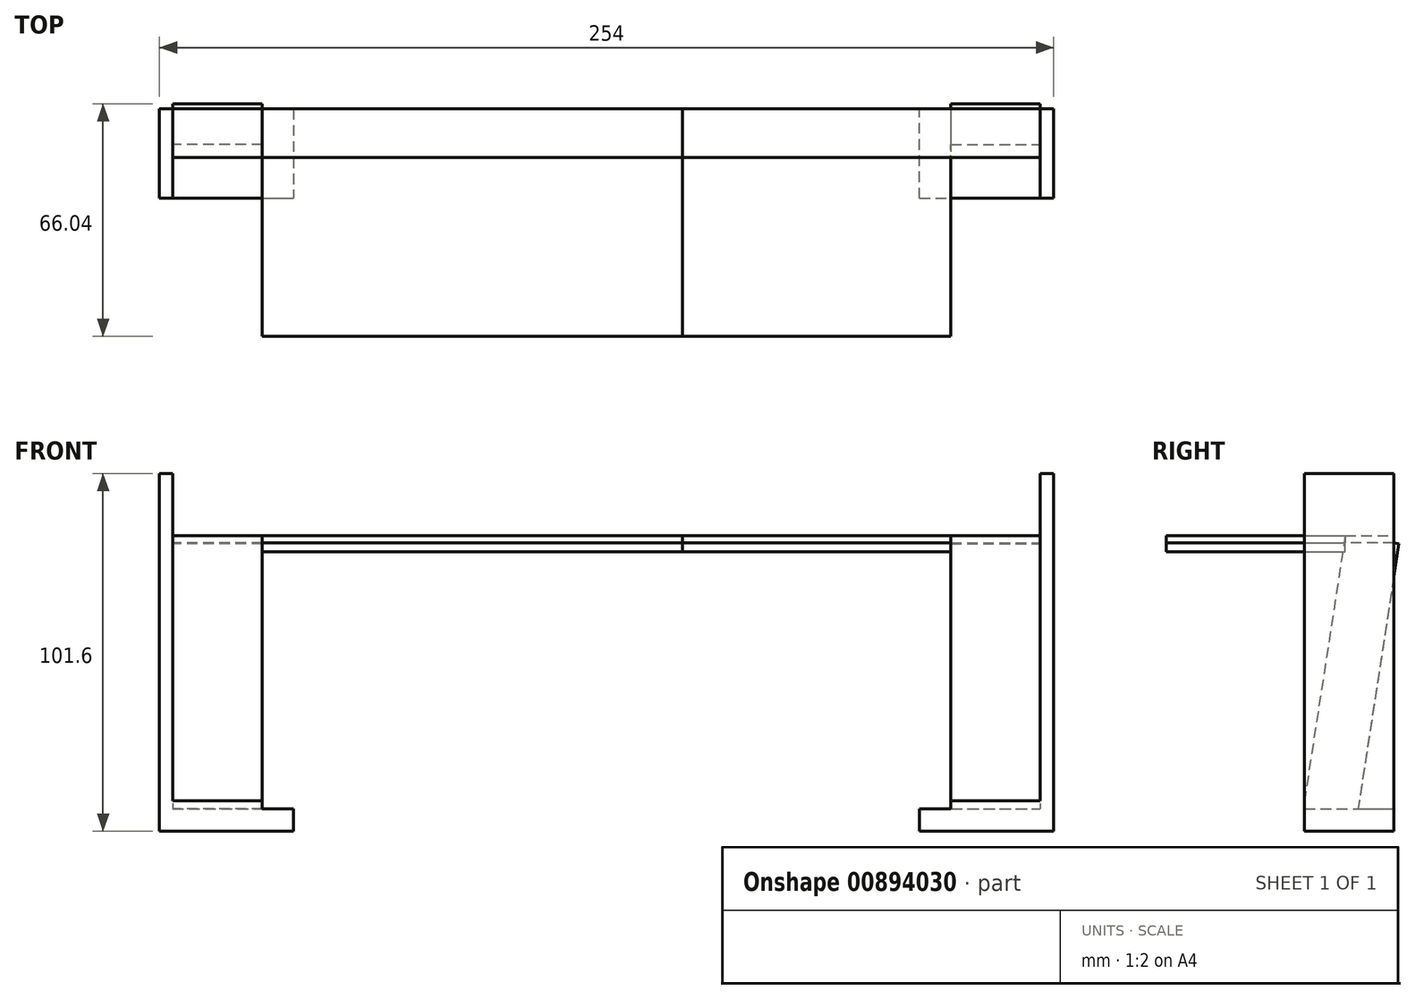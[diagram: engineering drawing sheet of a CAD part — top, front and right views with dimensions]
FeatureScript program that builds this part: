
annotation { "Feature Type Name" : "Feature", "Feature Type Description" : "" }
export const myFeature = defineFeature(function(context is Context, id is Id, definition is map)
    precondition{}
    {
        {
            var Q0;
            Q0=qCreatedBy(makeId("Top.planeOp"),FACE);
            var sketch = newSketch(context, id + "F0", { "sketchPlane" : qUnion([Q0])});
            skLineSegment(sketch, "E0.bottom", {"start": v(-148.04, 0) * mm, "end": v(-109.94, 0) * mm});
            skLineSegment(sketch, "E0.top", {"start": v(-148.04, -25.4) * mm, "end": v(-109.94, -25.4) * mm});
            skLineSegment(sketch, "E0.left", {"start": v(-148.04, 0) * mm, "end": v(-148.04, -25.4) * mm});
            skLineSegment(sketch, "E0.right", {"start": v(-109.94, 0) * mm, "end": v(-109.94, -25.4) * mm});
            skLineSegment(sketch, "E1", {"start": v(-109.94, -25.4) * mm, "end": v(67.86, -25.4) * mm});
            skLineSegment(sketch, "E2.bottom", {"start": v(67.86, -25.4) * mm, "end": v(105.96, -25.4) * mm});
            skLineSegment(sketch, "E2.top", {"start": v(67.86, 0) * mm, "end": v(105.96, 0) * mm});
            skLineSegment(sketch, "E2.left", {"start": v(67.86, -25.4) * mm, "end": v(67.86, 0) * mm});
            skLineSegment(sketch, "E2.right", {"start": v(105.96, -25.4) * mm, "end": v(105.96, 0) * mm});
            skLineSegment(sketch, "E3", {"start": v(-144.23, -12.7) * mm, "end": v(-144.23, 0) * mm});
            skLineSegment(sketch, "E4", {"start": v(-144.23, -12.7) * mm, "end": v(-144.23, -25.4) * mm});
            skLineSegment(sketch, "E5", {"start": v(102.15, -18.45) * mm, "end": v(102.15, 0) * mm});
            skLineSegment(sketch, "E6", {"start": v(102.15, -18.45) * mm, "end": v(102.15, -25.4) * mm});
            skSolve(sketch);
        }
        {
            var Q0;
            Q0=makeQuery(id+"F0.imprint","IMPRINT",FACE,{"disambiguationData":[TD([[makeQuery(id+"F0.imprint","IMPRINT",EDGE,{"derivedFrom":sQuery(id+"F0.wireOp",EDGE,"E0.bottom")}),-1.0]])]});
            extrude(context, id + "F1", {"entities" : qUnion([Q0]), "depth" : 6.35 * mm, "offsetDistance" : 25.4 * mm});
        }
        {
            var Q0;
            Q0=makeQuery(id+"F0.imprint","IMPRINT",FACE,{"disambiguationData":[TD([[makeQuery(id+"F0.imprint","IMPRINT",EDGE,{"derivedFrom":sQuery(id+"F0.wireOp",EDGE,"E2.bottom")}),1.0]])]});
            extrude(context, id + "F2", {"entities" : qUnion([Q0]), "depth" : 6.35 * mm, "offsetDistance" : 25.4 * mm});
        }
        {
            var Q0;
            {var subQ0=sQuery(id+"F0.wireOp",EDGE,"E0.left");Q0=makeQuery(id+"F0.imprint","IMPRINT",FACE,{"disambiguationData":[TD([[makeQuery(id+"F0.imprint","IMPRINT",EDGE,{"derivedFrom":subQ0}),1.0]])]});}
            extrude(context, id + "F3", {"entities" : qUnion([Q0]), "operationType" : NewBodyOperationType.ADD, "depth" : 25.4 * mm, "offsetDistance" : 25.4 * mm});
        }
        {
            var Q0;
            {var subQ0=sQuery(id+"F0.wireOp",EDGE,"E2.right");Q0=makeQuery(id+"F0.imprint","IMPRINT",FACE,{"disambiguationData":[TD([[makeQuery(id+"F0.imprint","IMPRINT",EDGE,{"derivedFrom":subQ0}),1.0]])]});}
            extrude(context, id + "F4", {"entities" : qUnion([Q0]), "operationType" : NewBodyOperationType.ADD, "depth" : 25.4 * mm, "offsetDistance" : 25.4 * mm});
        }
        {
            var Q0;
            Q0=makeQuery(id+"F3.opExtrude","SWEPT_FACE",FACE,{"disambiguationData":[OSD([sQuery(id+"F0.wireOp",EDGE,"E3"),sQuery(id+"F0.wireOp",EDGE,"E4")])]});
            var sketch = newSketch(context, id + "F5", { "sketchPlane" : qUnion([Q0])});
            skLineSegment(sketch, "E7", {"start": v(0, 6.35) * mm, "end": v(-10.16, 6.35) * mm});
            skLineSegment(sketch, "E8", {"start": v(-25.4, 6.35) * mm, "end": v(-20.32, 6.35) * mm});
            skLineSegment(sketch, "E9", {"start": v(-10.16, 6.35) * mm, "end": v(-25.4, 8.7) * mm});
            skSolve(sketch);
        }
        {
            var Q0;
            {var subQ0=sQuery(id+"F5.wireOp",EDGE,"E8");Q0=makeQuery(id+"F5.imprint","IMPRINT",FACE,{"disambiguationData":[TD([[makeQuery(id+"F5.imprint","IMPRINT",EDGE,{"derivedFrom":subQ0}),1.0]])]});}
            extrude(context, id + "F6", {"entities" : qUnion([Q0]), "operationType" : NewBodyOperationType.ADD, "depth" : 25.4 * mm, "offsetDistance" : 25.4 * mm});
        }
        {
            var Q0;
            Q0=makeQuery(id+"F4.opExtrude","SWEPT_FACE",FACE,{"disambiguationData":[OSD([sQuery(id+"F0.wireOp",EDGE,"E5"),sQuery(id+"F0.wireOp",EDGE,"E6")])]});
            var sketch = newSketch(context, id + "F7", { "sketchPlane" : qUnion([Q0])});
            skLineSegment(sketch, "E10", {"start": v(0, 6.35) * mm, "end": v(10.16, 6.35) * mm});
            skLineSegment(sketch, "E11", {"start": v(10.16, 6.35) * mm, "end": v(25.4, 8.7) * mm});
            skSolve(sketch);
        }
        {
            var Q0;
            {var subQ0=sQuery(id+"F7.wireOp",EDGE,"E11");Q0=makeQuery(id+"F7.imprint","IMPRINT",FACE,{"disambiguationData":[TD([[makeQuery(id+"F7.imprint","IMPRINT",EDGE,{"derivedFrom":subQ0}),-1.0]])]});}
            extrude(context, id + "F8", {"entities" : qUnion([Q0]), "operationType" : NewBodyOperationType.ADD, "depth" : 25.4 * mm, "offsetDistance" : 25.4 * mm});
        }
        {
            var Q0;
            Q0=makeQuery(id+"F6.opExtrude","SWEPT_FACE",FACE,{"disambiguationData":[OSD([sQuery(id+"F5.wireOp",EDGE,"E9")])]});
            var sketch = newSketch(context, id + "F9", { "sketchPlane" : qUnion([Q0])});
            skSolve(sketch);
        }
        {
            var Q0;
            Q0=makeQuery(id+"F8.opExtrude","SWEPT_FACE",FACE,{"disambiguationData":[OSD([sQuery(id+"F7.wireOp",EDGE,"E11")])]});
            var sketch = newSketch(context, id + "F10", { "sketchPlane" : qUnion([Q0])});
            skSolve(sketch);
        }
        {
            var Q0;
            {var subQ0=sQuery(id+"F7.wireOp",EDGE,"E11");Q0=makeQuery(id+"F10.imprint","IMPRINT",FACE,{"disambiguationData":[TD([[makeQuery(id+"F10.imprint","IMPRINT",EDGE,{"derivedFrom":makeQuery(id+"F8.opExtrude","CAP_EDGE",EDGE,{"disambiguationData":[OSD([subQ0])],"isStart":false})}),1.0]])]});}
            extrude(context, id + "F11", {"entities" : qUnion([Q0]), "operationType" : NewBodyOperationType.ADD, "depth" : 76.2 * mm, "offsetDistance" : 25.4 * mm});
        }
        {
            var Q0;
            {var subQ0=sQuery(id+"F5.wireOp",EDGE,"E9");Q0=makeQuery(id+"F9.imprint","IMPRINT",FACE,{"disambiguationData":[TD([[makeQuery(id+"F9.imprint","IMPRINT",EDGE,{"derivedFrom":makeQuery(id+"F6.opExtrude","CAP_EDGE",EDGE,{"disambiguationData":[OSD([subQ0])],"isStart":false})}),-1.0]])]});}
            extrude(context, id + "F12", {"entities" : qUnion([Q0]), "operationType" : NewBodyOperationType.ADD, "depth" : 76.2 * mm, "offsetDistance" : 25.4 * mm});
        }
        {
            var Q0;
            Q0=makeQuery(id+"F4.opExtrude","CAP_FACE",FACE,{"disambiguationData":[OSD([sQuery(id+"F0.wireOp",EDGE,"E2.bottom"),sQuery(id+"F0.wireOp",EDGE,"E2.top"),sQuery(id+"F0.wireOp",EDGE,"E2.right"),sQuery(id+"F0.wireOp",EDGE,"E5"),sQuery(id+"F0.wireOp",EDGE,"E6")])],"isStart":false});
            var sketch = newSketch(context, id + "F13", { "sketchPlane" : qUnion([Q0])});
            skSolve(sketch);
        }
        {
            var Q0;
            {var subQ4=sQuery(id+"F0.wireOp",EDGE,"E2.bottom");Q0=makeQuery(id+"F13.imprint","IMPRINT",FACE,{"disambiguationData":[TD([[makeQuery(id+"F13.imprint","IMPRINT",EDGE,{"derivedFrom":makeQuery(id+"F4.opExtrude","CAP_EDGE",EDGE,{"disambiguationData":[OSD([subQ4])],"isStart":false})}),1.0]])]});}
            extrude(context, id + "F14", {"entities" : qUnion([Q0]), "operationType" : NewBodyOperationType.ADD, "depth" : 76.2 * mm, "offsetDistance" : 25.4 * mm});
        }
        {
            var Q0;
            Q0=makeQuery(id+"F3.opExtrude","CAP_FACE",FACE,{"disambiguationData":[OSD([sQuery(id+"F0.wireOp",EDGE,"E0.bottom"),sQuery(id+"F0.wireOp",EDGE,"E0.top"),sQuery(id+"F0.wireOp",EDGE,"E0.left"),sQuery(id+"F0.wireOp",EDGE,"E3"),sQuery(id+"F0.wireOp",EDGE,"E4")])],"isStart":false});
            var sketch = newSketch(context, id + "F15", { "sketchPlane" : qUnion([Q0])});
            skSolve(sketch);
        }
        {
            var Q0;
            {var subQ4=sQuery(id+"F0.wireOp",EDGE,"E0.bottom");Q0=makeQuery(id+"F15.imprint","IMPRINT",FACE,{"disambiguationData":[TD([[makeQuery(id+"F15.imprint","IMPRINT",EDGE,{"derivedFrom":makeQuery(id+"F3.opExtrude","CAP_EDGE",EDGE,{"disambiguationData":[OSD([subQ4])],"isStart":false})}),-1.0]])]});}
            extrude(context, id + "F16", {"entities" : qUnion([Q0]), "operationType" : NewBodyOperationType.ADD, "depth" : 76.2 * mm, "offsetDistance" : 25.4 * mm});
        }
        {
            var Q0;
            {var subQ0=sQuery(id+"F0.wireOp",EDGE,"E6");var subQ1=sQuery(id+"F0.wireOp",EDGE,"E5");var subQ2=sQuery(id+"F0.wireOp",EDGE,"E2.bottom");Q0=makeQuery(id+"F14.boolean.opBoolean","MERGE",FACE,{"derivedFrom":[makeQuery(id+"F11.boolean.opBoolean","SPLIT",FACE,{"disambiguationData":[TD([makeQuery(id+"F2.opExtrude","SWEPT_FACE",FACE,{"disambiguationData":[OSD([subQ2])]})])],"derivedFrom":makeQuery(id+"F4.opExtrude","SWEPT_FACE",FACE,{"disambiguationData":[OSD([subQ1,subQ0])]})}),makeQuery(id+"F14.opExtrude","SWEPT_FACE",FACE,{"disambiguationData":[OSD([subQ1,subQ0])]})]});}
            var sketch = newSketch(context, id + "F17", { "sketchPlane" : qUnion([Q0])});
            skLineSegment(sketch, "E12", {"start": v(13.8, 84) * mm, "end": v(0, 84) * mm});
            skLineSegment(sketch, "E13", {"start": v(0, 84) * mm, "end": v(0, 81.88) * mm});
            skSolve(sketch);
        }
        {
            var Q0;
            Q0=makeQuery(id+"F17.imprint","IMPRINT",FACE,{"disambiguationData":[TD([[makeQuery(id+"F17.imprint","IMPRINT",EDGE,{"derivedFrom":sQuery(id+"F17.wireOp",EDGE,"E12")}),1.0]])]});
            extrude(context, id + "F18", {"entities" : qUnion([Q0]), "operationType" : NewBodyOperationType.ADD, "depth" : 25.4 * mm, "offsetDistance" : 25.4 * mm});
        }
        {
            var Q0;
            {var subQ0=sQuery(id+"F0.wireOp",EDGE,"E4");var subQ1=sQuery(id+"F0.wireOp",EDGE,"E3");var subQ2=sQuery(id+"F0.wireOp",EDGE,"E0.top");Q0=makeQuery(id+"F16.boolean.opBoolean","MERGE",FACE,{"derivedFrom":[makeQuery(id+"F12.boolean.opBoolean","SPLIT",FACE,{"disambiguationData":[TD([makeQuery(id+"F1.opExtrude","SWEPT_FACE",FACE,{"disambiguationData":[OSD([subQ2])]})])],"derivedFrom":makeQuery(id+"F3.opExtrude","SWEPT_FACE",FACE,{"disambiguationData":[OSD([subQ1,subQ0])]})}),makeQuery(id+"F16.opExtrude","SWEPT_FACE",FACE,{"disambiguationData":[OSD([subQ1,subQ0])]})]});}
            var sketch = newSketch(context, id + "F19", { "sketchPlane" : qUnion([Q0])});
            skLineSegment(sketch, "E14", {"start": v(0, 84) * mm, "end": v(0, 81.88) * mm});
            skLineSegment(sketch, "E15", {"start": v(0, 84) * mm, "end": v(-13.8, 84) * mm});
            skSolve(sketch);
        }
        {
            var Q0;
            {var subQ0=sQuery(id+"F7.wireOp",EDGE,"E11");Q0=makeQuery(id+"F18.boolean.opBoolean","MERGE",FACE,{"derivedFrom":[makeQuery(id+"F11.boolean.opBoolean","MERGE",FACE,{"derivedFrom":[makeQuery(id+"F8.opExtrude","CAP_FACE",FACE,{"disambiguationData":[OSD([sQuery(id+"F0.wireOp",EDGE,"E2.bottom"),sQuery(id+"F0.wireOp",EDGE,"E2.top"),sQuery(id+"F0.wireOp",EDGE,"E2.left"),sQuery(id+"F0.wireOp",EDGE,"E2.right"),sQuery(id+"F0.wireOp",EDGE,"E5"),sQuery(id+"F0.wireOp",EDGE,"E6"),subQ0])],"isStart":false}),makeQuery(id+"F11.opExtrude","SWEPT_FACE",FACE,{"disambiguationData":[OSD([subQ0]),TDD([makeQuery(id+"F10.imprint","IMPRINT",EDGE,{"derivedFrom":makeQuery(id+"F8.opExtrude","CAP_EDGE",EDGE,{"disambiguationData":[OSD([subQ0])],"isStart":false})})])]})]}),makeQuery(id+"F18.opExtrude","CAP_FACE",FACE,{"disambiguationData":[OSD([subQ0,sQuery(id+"F17.wireOp",EDGE,"E12"),sQuery(id+"F17.wireOp",EDGE,"E13")])],"isStart":false})]});}
            var sketch = newSketch(context, id + "F20", { "sketchPlane" : qUnion([Q0])});
            skLineSegment(sketch, "E16", {"start": v(0, 81.88) * mm, "end": v(13.8, 81.88) * mm});
            skLineSegment(sketch, "E17", {"start": v(0, 81.88) * mm, "end": v(0, 84) * mm});
            skLineSegment(sketch, "E18", {"start": v(0, 84) * mm, "end": v(13.8, 84) * mm});
            skLineSegment(sketch, "E19", {"start": v(13.8, 84) * mm, "end": v(13.8, 81.88) * mm});
            skSolve(sketch);
        }
        {
            var Q0;
            Q0 = qSketchRegion(id + "F20", true);
            extrude(context, id + "F21", {"entities" : qUnion([Q0]), "operationType" : NewBodyOperationType.ADD, "depth" : 76.2 * mm, "offsetDistance" : 25.4 * mm});
        }
        {
            var Q0;
            Q0=makeQuery(id+"F19.imprint","IMPRINT",FACE,{"disambiguationData":[TD([[makeQuery(id+"F19.imprint","IMPRINT",EDGE,{"derivedFrom":sQuery(id+"F19.wireOp",EDGE,"E14")}),-1.0]])]});
            extrude(context, id + "F22", {"entities" : qUnion([Q0]), "operationType" : NewBodyOperationType.ADD, "depth" : 25.4 * mm, "offsetDistance" : 25.4 * mm});
        }
        {
            var Q0;
            {var subQ0=sQuery(id+"F5.wireOp",EDGE,"E9");Q0=makeQuery(id+"F22.boolean.opBoolean","MERGE",FACE,{"derivedFrom":[makeQuery(id+"F12.boolean.opBoolean","MERGE",FACE,{"derivedFrom":[makeQuery(id+"F6.opExtrude","CAP_FACE",FACE,{"disambiguationData":[OSD([sQuery(id+"F0.wireOp",EDGE,"E0.bottom"),sQuery(id+"F0.wireOp",EDGE,"E0.top"),sQuery(id+"F0.wireOp",EDGE,"E0.left"),sQuery(id+"F0.wireOp",EDGE,"E0.right"),sQuery(id+"F0.wireOp",EDGE,"E3"),sQuery(id+"F0.wireOp",EDGE,"E4"),sQuery(id+"F5.wireOp",EDGE,"E8"),subQ0])],"isStart":false}),makeQuery(id+"F12.opExtrude","SWEPT_FACE",FACE,{"disambiguationData":[OSD([subQ0]),TDD([makeQuery(id+"F9.imprint","IMPRINT",EDGE,{"derivedFrom":makeQuery(id+"F6.opExtrude","CAP_EDGE",EDGE,{"disambiguationData":[OSD([subQ0])],"isStart":false})})])]})]}),makeQuery(id+"F22.opExtrude","CAP_FACE",FACE,{"disambiguationData":[OSD([subQ0,sQuery(id+"F19.wireOp",EDGE,"E14"),sQuery(id+"F19.wireOp",EDGE,"E15")])],"isStart":false})]});}
            var sketch = newSketch(context, id + "F23", { "sketchPlane" : qUnion([Q0])});
            skLineSegment(sketch, "E20", {"start": v(0, 81.88) * mm, "end": v(-13.8, 81.88) * mm});
            skLineSegment(sketch, "E21", {"start": v(-13.8, 81.88) * mm, "end": v(-13.8, 84) * mm});
            skSolve(sketch);
        }
        {
            var Q0;
            Q0=makeQuery(id+"F23.imprint","IMPRINT",FACE,{"disambiguationData":[TD([[makeQuery(id+"F23.imprint","IMPRINT",EDGE,{"derivedFrom":sQuery(id+"F23.wireOp",EDGE,"E20")}),-1.0]])]});
            extrude(context, id + "F24", {"entities" : qUnion([Q0]), "depth" : 119.38 * mm, "offsetDistance" : 25.4 * mm});
        }
        {
            var Q0;
            Q0=makeQuery(id+"F24.opExtrude","SWEPT_FACE",FACE,{"disambiguationData":[OSD([sQuery(id+"F23.wireOp",EDGE,"E21")])]});
            extrude(context, id + "F25", {"entities" : qUnion([Q0]), "depth" : 50.8 * mm, "offsetDistance" : 25.4 * mm});
        }
        {
            var Q0;
            Q0=makeQuery(id+"F21.opExtrude","SWEPT_FACE",FACE,{"disambiguationData":[OSD([sQuery(id+"F20.wireOp",EDGE,"E19")])]});
            extrude(context, id + "F26", {"entities" : qUnion([Q0]), "depth" : 50.8 * mm, "offsetDistance" : 25.4 * mm});
        }
        {
            var Q0;
            Q0=makeQuery(id+"F26.opExtrude","SWEPT_FACE",FACE,{"disambiguationData":[OSD([sQuery(id+"F20.wireOp",EDGE,"E16"),sQuery(id+"F20.wireOp",EDGE,"E19")])]});
            extrude(context, id + "F27", {"entities" : qUnion([Q0]), "depth" : 2.54 * mm, "offsetDistance" : 25.4 * mm});
        }
        {
            var Q0;
            Q0=makeQuery(id+"F25.opExtrude","SWEPT_FACE",FACE,{"disambiguationData":[OSD([sQuery(id+"F23.wireOp",EDGE,"E20"),sQuery(id+"F23.wireOp",EDGE,"E21")])]});
            extrude(context, id + "F28", {"entities" : qUnion([Q0]), "depth" : 2.54 * mm, "offsetDistance" : 25.4 * mm});
        }
    });
